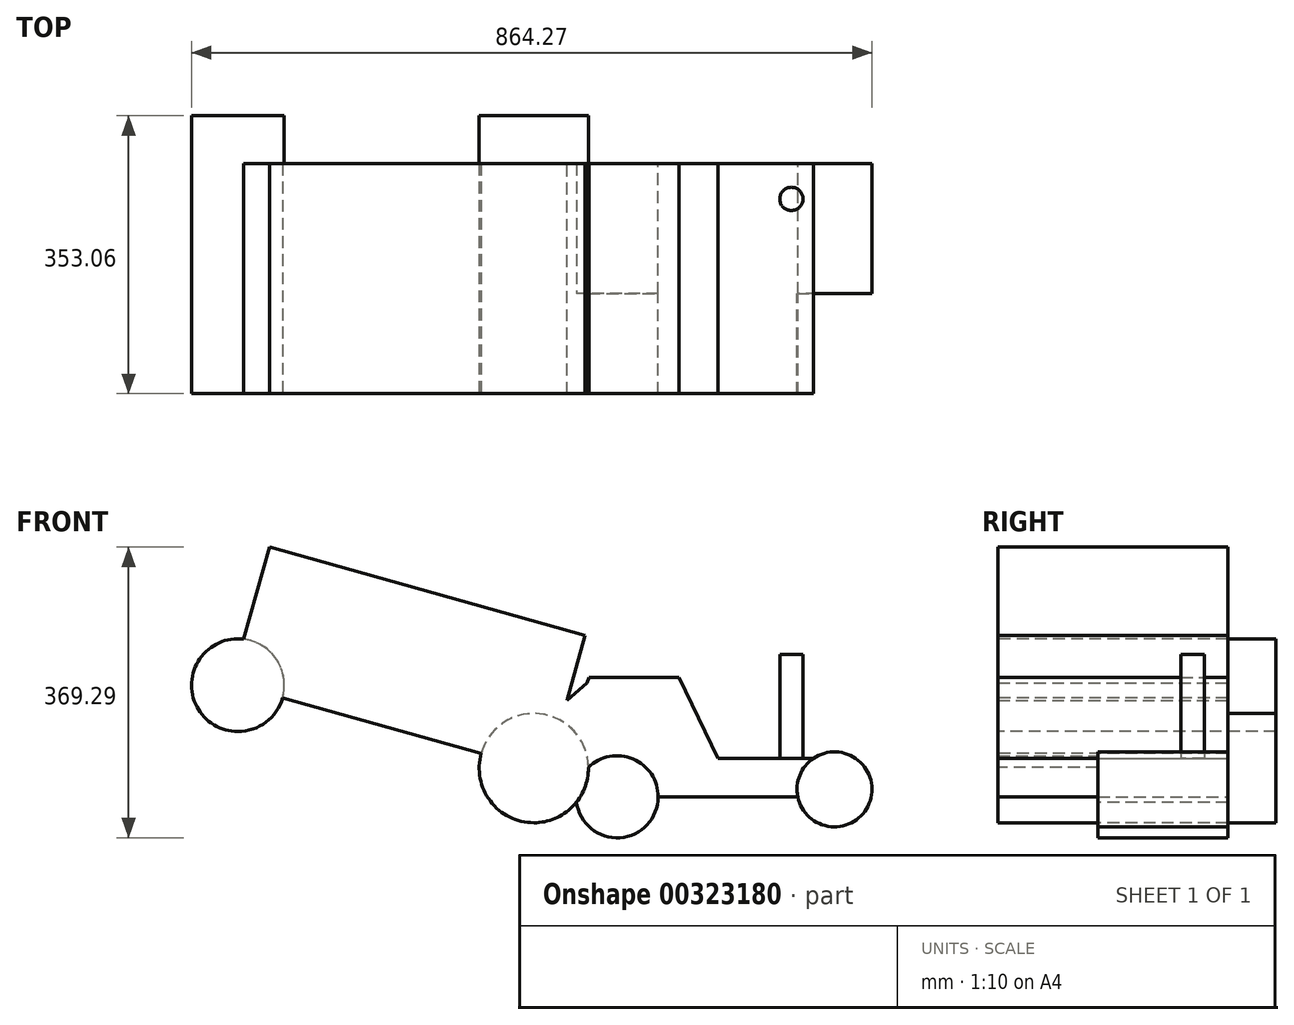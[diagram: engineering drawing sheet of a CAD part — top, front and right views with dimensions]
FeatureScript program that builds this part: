
annotation { "Feature Type Name" : "Feature", "Feature Type Description" : "" }
export const myFeature = defineFeature(function(context is Context, id is Id, definition is map)
    precondition{}
    {
        {
            var Q0;
            Q0=qCreatedBy(makeId("Front.planeOp"),FACE);
            var sketch = newSketch(context, id + "F0", { "sketchPlane" : qUnion([Q0])});
            skLineSegment(sketch, "E0", {"start": v(-174.5, 12.35) * mm, "end": v(-143.4, 68.5) * mm});
            skLineSegment(sketch, "E1", {"start": v(-143.4, 68.5) * mm, "end": v(-33.77, 68.5) * mm});
            skLineSegment(sketch, "E2", {"start": v(-33.77, 68.5) * mm, "end": v(8.95, 17.89) * mm});
            skLineSegment(sketch, "E3", {"start": v(8.95, 17.89) * mm, "end": v(131.06, 17.89) * mm});
            skLineSegment(sketch, "E4", {"start": v(131.06, 17.89) * mm, "end": v(200.97, 17.89) * mm});
            skLineSegment(sketch, "E5", {"start": v(200.97, 17.89) * mm, "end": v(200.97, -30.85) * mm});
            skLineSegment(sketch, "E6", {"start": v(200.97, -30.85) * mm, "end": v(29.07, -30.85) * mm});
            skLineSegment(sketch, "E7", {"start": v(29.07, -30.85) * mm, "end": v(8.95, 17.89) * mm});
            skLineSegment(sketch, "E8", {"start": v(-88.58, 68.5) * mm, "end": v(-88.58, -30.85) * mm});
            skLineSegment(sketch, "E9", {"start": v(-88.58, -30.85) * mm, "end": v(29.07, -30.85) * mm});
            skLineSegment(sketch, "E10", {"start": v(-88.58, -30.85) * mm, "end": v(-174.5, 12.35) * mm});
            skLineSegment(sketch, "E11", {"start": v(-143.4, 68.5) * mm, "end": v(-124.67, 120.46) * mm});
            skLineSegment(sketch, "E12", {"start": v(-124.67, 120.46) * mm, "end": v(-10.3, 120.46) * mm});
            skLineSegment(sketch, "E13", {"start": v(-10.3, 120.46) * mm, "end": v(-33.77, 68.5) * mm});
            skLineSegment(sketch, "E14", {"start": v(-10.3, 120.46) * mm, "end": v(39.23, 17.89) * mm});
            skLineSegment(sketch, "E15", {"start": v(-174.5, 12.35) * mm, "end": v(-152.27, 91.63) * mm});
            skLineSegment(sketch, "E16", {"start": v(-152.27, 91.63) * mm, "end": v(-119.25, 120.46) * mm});
            skSolve(sketch);
        }
        {
            var Q0;
            Q0 = qSketchRegion(id + "F0", true);
            extrude(context, id + "F1", {"entities" : qUnion([Q0]), "depth" : 114.3 * mm});
        }
        {
            var Q0;
            Q0=makeQuery(id+"F1.opExtrude","SWEPT_FACE",FACE,{"disambiguationData":[OSD([sQuery(id+"F0.wireOp",EDGE,"E3"),sQuery(id+"F0.wireOp",EDGE,"E4")])]});
            var sketch = newSketch(context, id + "F2", { "sketchPlane" : qUnion([Q0])});
            skCircle(sketch, "E17", {"center": v(132.66, -44.75) * mm, "radius": 14.76 * mm});
            skSolve(sketch);
        }
        {
            var Q0;
            Q0 = qSketchRegion(id + "F2", true);
            extrude(context, id + "F3", {"entities" : qUnion([Q0]), "operationType" : NewBodyOperationType.ADD, "depth" : 132.08 * mm});
        }
        {
            var Q0;
            Q0=makeQuery(id+"F1.opExtrude","CAP_FACE",FACE,{"disambiguationData":[OSD([sQuery(id+"F0.wireOp",EDGE,"E3"),sQuery(id+"F0.wireOp",EDGE,"E4"),sQuery(id+"F0.wireOp",EDGE,"E5"),sQuery(id+"F0.wireOp",EDGE,"E6"),sQuery(id+"F0.wireOp",EDGE,"E9"),sQuery(id+"F0.wireOp",EDGE,"E10"),sQuery(id+"F0.wireOp",EDGE,"E11"),sQuery(id+"F0.wireOp",EDGE,"E12"),sQuery(id+"F0.wireOp",EDGE,"E14"),sQuery(id+"F0.wireOp",EDGE,"E15"),sQuery(id+"F0.wireOp",EDGE,"E16")])],"isStart":true});
            var sketch = newSketch(context, id + "F4", { "sketchPlane" : qUnion([Q0])});
            skLineSegment(sketch, "E18", {"start": v(-200.97, -30.85) * mm, "end": v(88.58, -30.85) * mm});
            skCircle(sketch, "E19", {"center": v(-187.45, -21.44) * mm, "radius": 47.6 * mm});
            skCircle(sketch, "E20", {"center": v(88.58, -30.85) * mm, "radius": 52.12 * mm});
            skSolve(sketch);
        }
        {
            var Q0;
            Q0 = qSketchRegion(id + "F4", true);
            extrude(context, id + "F5", {"entities" : qUnion([Q0]), "operationType" : NewBodyOperationType.ADD, "oppositeDirection" : true, "depth" : 165.1 * mm});
        }
        {
            var Q0;
            Q0=makeQuery(id+"F1.opExtrude","CAP_FACE",FACE,{"disambiguationData":[OSD([sQuery(id+"F0.wireOp",EDGE,"E3"),sQuery(id+"F0.wireOp",EDGE,"E4"),sQuery(id+"F0.wireOp",EDGE,"E5"),sQuery(id+"F0.wireOp",EDGE,"E6"),sQuery(id+"F0.wireOp",EDGE,"E9"),sQuery(id+"F0.wireOp",EDGE,"E10"),sQuery(id+"F0.wireOp",EDGE,"E11"),sQuery(id+"F0.wireOp",EDGE,"E12"),sQuery(id+"F0.wireOp",EDGE,"E14"),sQuery(id+"F0.wireOp",EDGE,"E15"),sQuery(id+"F0.wireOp",EDGE,"E16")])],"isStart":false});
            extrude(context, id + "F6", {"entities" : qUnion([Q0]), "operationType" : NewBodyOperationType.ADD, "depth" : 53.34 * mm});
        }
        {
            var Q0;
            {var subQ0=sQuery(id+"F0.wireOp",EDGE,"E15");Q0=makeQuery(id+"F6.boolean.opBoolean","MERGE",FACE,{"derivedFrom":[makeQuery(id+"F1.opExtrude","SWEPT_FACE",FACE,{"disambiguationData":[OSD([subQ0])]}),makeQuery(id+"F6.opExtrude","SWEPT_FACE",FACE,{"disambiguationData":[OSD([subQ0])]})]});}
            var sketch = newSketch(context, id + "F7", { "sketchPlane" : qUnion([Q0])});
            skLineSegment(sketch, "E21.bottom", {"start": v(0, 28.4) * mm, "end": v(167.64, 28.4) * mm});
            skLineSegment(sketch, "E21.top", {"start": v(0, -47.16) * mm, "end": v(167.64, -47.16) * mm});
            skLineSegment(sketch, "E21.left", {"start": v(0, 28.4) * mm, "end": v(0, -47.16) * mm});
            skLineSegment(sketch, "E21.right", {"start": v(167.64, 28.4) * mm, "end": v(167.64, -47.16) * mm});
            skSolve(sketch);
        }
        {
            var Q0;
            Q0 = qSketchRegion(id + "F7", true);
            extrude(context, id + "F8", {"entities" : qUnion([Q0]), "operationType" : NewBodyOperationType.ADD, "depth" : 416.56 * mm});
        }
        {
            var Q0;
            Q0=makeQuery(id+"F8.opExtrude","SWEPT_FACE",FACE,{"disambiguationData":[OSD([sQuery(id+"F7.wireOp",EDGE,"E21.bottom")])]});
            extrude(context, id + "F9", {"entities" : qUnion([Q0]), "operationType" : NewBodyOperationType.ADD, "depth" : 104.14 * mm});
        }
        {
            var Q0;
            {var subQ0=sQuery(id+"F7.wireOp",EDGE,"E21.right");var subQ1=sQuery(id+"F0.wireOp",EDGE,"E15");Q0=makeQuery(id+"F9.boolean.opBoolean","MERGE",FACE,{"derivedFrom":[makeQuery(id+"F8.boolean.opBoolean","MERGE",FACE,{"derivedFrom":[makeQuery(id+"F6.opExtrude","CAP_FACE",FACE,{"disambiguationData":[OSD([sQuery(id+"F0.wireOp",EDGE,"E3"),sQuery(id+"F0.wireOp",EDGE,"E4"),sQuery(id+"F0.wireOp",EDGE,"E5"),sQuery(id+"F0.wireOp",EDGE,"E6"),sQuery(id+"F0.wireOp",EDGE,"E9"),sQuery(id+"F0.wireOp",EDGE,"E10"),sQuery(id+"F0.wireOp",EDGE,"E11"),sQuery(id+"F0.wireOp",EDGE,"E12"),sQuery(id+"F0.wireOp",EDGE,"E14"),subQ1,sQuery(id+"F0.wireOp",EDGE,"E16")])],"isStart":false}),makeQuery(id+"F8.opExtrude","SWEPT_FACE",FACE,{"disambiguationData":[OSD([subQ0])]})]}),makeQuery(id+"F9.opExtrude","SWEPT_FACE",FACE,{"disambiguationData":[OSD([subQ1,sQuery(id+"F7.wireOp",EDGE,"E21.bottom"),subQ0])]})]});}
            var sketch = newSketch(context, id + "F10", { "sketchPlane" : qUnion([Q0])});
            skCircle(sketch, "E22", {"center": v(-570.31, 110.92) * mm, "radius": 58.9 * mm});
            skCircle(sketch, "E23", {"center": v(-194.5, 5.56) * mm, "radius": 69.36 * mm});
            skSolve(sketch);
        }
        {
            var Q0;
            Q0 = qSketchRegion(id + "F10", true);
            extrude(context, id + "F11", {"entities" : qUnion([Q0]), "operationType" : NewBodyOperationType.ADD, "oppositeDirection" : true, "depth" : 228.6 * mm});
        }
        {
            var Q0;
            {var subQ0=sQuery(id+"F7.wireOp",EDGE,"E21.right");var subQ1=sQuery(id+"F0.wireOp",EDGE,"E15");Q0=makeQuery(id+"F11.boolean.opBoolean","MERGE",FACE,{"derivedFrom":[makeQuery(id+"F9.boolean.opBoolean","MERGE",FACE,{"derivedFrom":[makeQuery(id+"F8.boolean.opBoolean","MERGE",FACE,{"derivedFrom":[makeQuery(id+"F6.opExtrude","CAP_FACE",FACE,{"disambiguationData":[OSD([sQuery(id+"F0.wireOp",EDGE,"E3"),sQuery(id+"F0.wireOp",EDGE,"E4"),sQuery(id+"F0.wireOp",EDGE,"E5"),sQuery(id+"F0.wireOp",EDGE,"E6"),sQuery(id+"F0.wireOp",EDGE,"E9"),sQuery(id+"F0.wireOp",EDGE,"E10"),sQuery(id+"F0.wireOp",EDGE,"E11"),sQuery(id+"F0.wireOp",EDGE,"E12"),sQuery(id+"F0.wireOp",EDGE,"E14"),subQ1,sQuery(id+"F0.wireOp",EDGE,"E16")])],"isStart":false}),makeQuery(id+"F8.opExtrude","SWEPT_FACE",FACE,{"disambiguationData":[OSD([subQ0])]})]}),makeQuery(id+"F9.opExtrude","SWEPT_FACE",FACE,{"disambiguationData":[OSD([subQ1,sQuery(id+"F7.wireOp",EDGE,"E21.bottom"),subQ0])]})]}),makeQuery(id+"F11.opExtrude","CAP_FACE",FACE,{"disambiguationData":[OSD([sQuery(id+"F10.wireOp",EDGE,"E22")])],"isStart":true}),makeQuery(id+"F11.opExtrude","CAP_FACE",FACE,{"disambiguationData":[OSD([sQuery(id+"F10.wireOp",EDGE,"E23")])],"isStart":true})]});}
            extrude(context, id + "F12", {"entities" : qUnion([Q0]), "operationType" : NewBodyOperationType.ADD, "depth" : 124.46 * mm});
        }
    });
